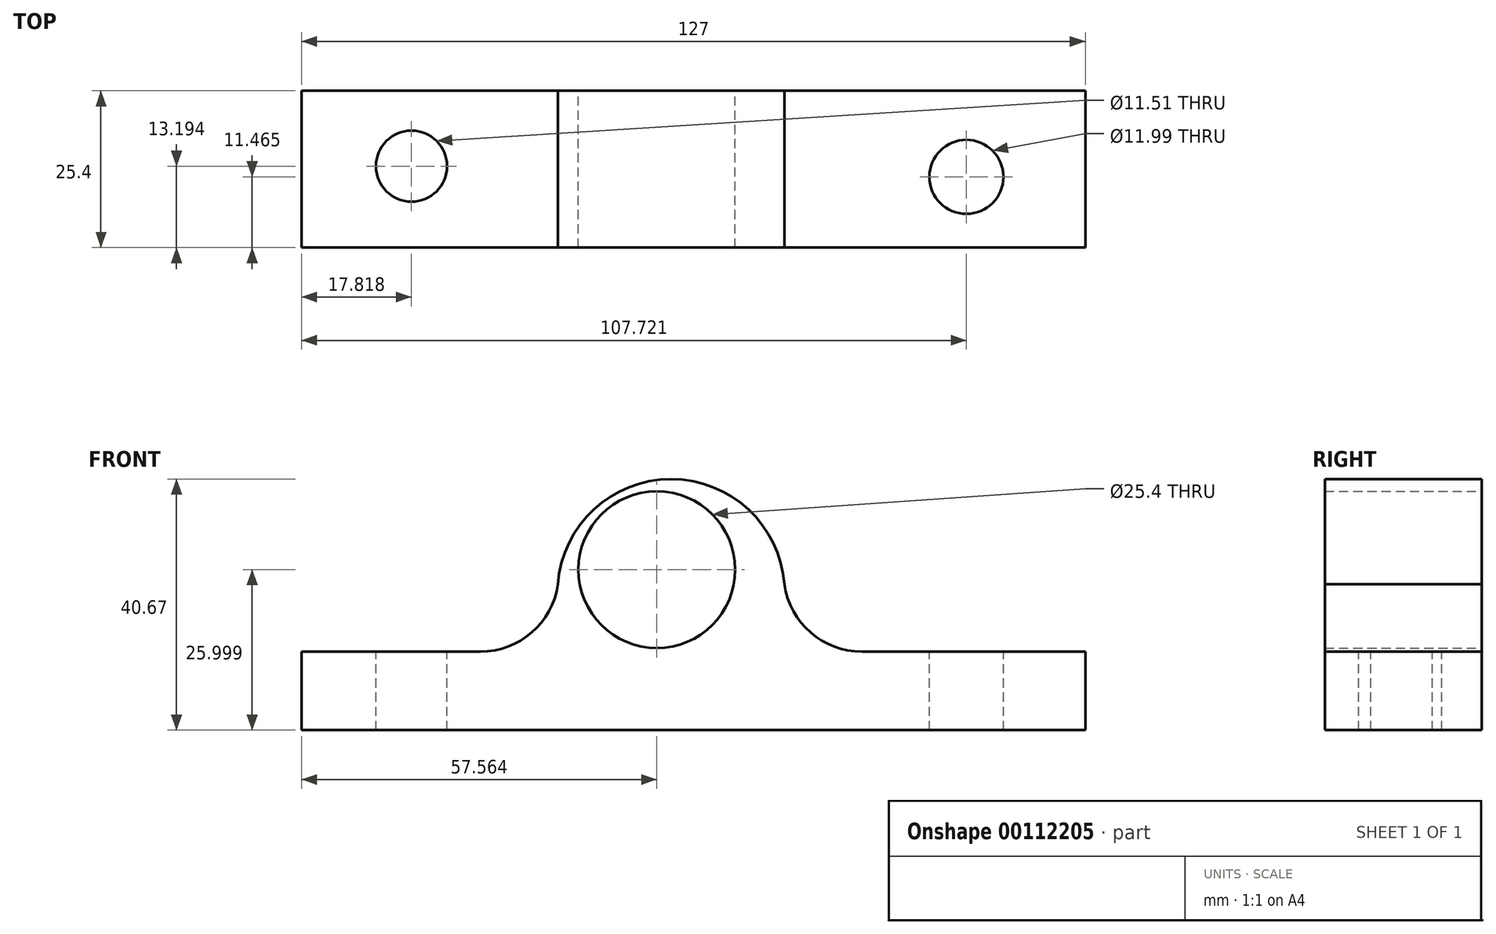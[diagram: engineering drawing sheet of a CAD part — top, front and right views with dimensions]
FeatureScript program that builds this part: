
annotation { "Feature Type Name" : "Feature", "Feature Type Description" : "" }
export const myFeature = defineFeature(function(context is Context, id is Id, definition is map)
    precondition{}
    {
        {
            var Q0;
            Q0=qCreatedBy(makeId("Front.planeOp"),FACE);
            var sketch = newSketch(context, id + "F0", { "sketchPlane" : qUnion([Q0])});
            skLineSegment(sketch, "E0", {"start": v(-62.5, -9.62) * mm, "end": v(-62.5, -22.32) * mm});
            skLineSegment(sketch, "E1", {"start": v(-62.5, -22.32) * mm, "end": v(64.5, -22.32) * mm});
            skLineSegment(sketch, "E2", {"start": v(64.5, -22.32) * mm, "end": v(64.5, -9.62) * mm});
            skLineSegment(sketch, "E3", {"start": v(64.5, -9.62) * mm, "end": v(28.3, -9.62) * mm});
            skLineSegment(sketch, "E4", {"start": v(-62.5, -9.62) * mm, "end": v(-33.54, -9.62) * mm});
            skArc(sketch, "E5.filletArc", {"start": v(-33.54, -9.62) * mm, "mid": v(-25.2, -6.5) * mm, "end": v(-20.96, 1.32) * mm});
            skArc(sketch, "E6.filletArc", {"start": v(15.73, 1.32) * mm, "mid": v(19.97, -6.5) * mm, "end": v(28.3, -9.62) * mm});
            skArc(sketch, "E7", {"start": v(15.73, 1.32) * mm, "mid": v(-2.62, 18.35) * mm, "end": v(-20.96, 1.32) * mm});
            skCircle(sketch, "E8", {"center": v(-4.94, 3.68) * mm, "radius": 12.7 * mm});
            skSolve(sketch);
        }
        {
            var Q0;
            Q0 = qSketchRegion(id + "F0", true);
            extrude(context, id + "F1", {"entities" : qUnion([Q0]), "depth" : 25.4 * mm});
        }
        {
            var Q0;
            Q0=makeQuery(id+"F1.opExtrude","SWEPT_FACE",FACE,{"disambiguationData":[OSD([sQuery(id+"F0.wireOp",EDGE,"E4")])]});
            var sketch = newSketch(context, id + "F2", { "sketchPlane" : qUnion([Q0])});
            skCircle(sketch, "E9", {"center": v(-44.68, -12.2) * mm, "radius": 5.75 * mm});
            skSolve(sketch);
        }
        {
            var Q0;
            Q0=makeQuery(id+"F1.opExtrude","SWEPT_FACE",FACE,{"disambiguationData":[OSD([sQuery(id+"F0.wireOp",EDGE,"E3")])]});
            var sketch = newSketch(context, id + "F3", { "sketchPlane" : qUnion([Q0])});
            skCircle(sketch, "E10", {"center": v(45.22, -13.94) * mm, "radius": 6 * mm});
            skSolve(sketch);
        }
        {
            var Q0;
            Q0 = qSketchRegion(id + "F2", true);
            extrude(context, id + "F4", {"entities" : qUnion([Q0]), "operationType" : NewBodyOperationType.REMOVE, "oppositeDirection" : true, "depth" : 25.4 * mm});
        }
        {
            var Q0;
            Q0=makeQuery(id+"F3.imprint","IMPRINT",FACE,{"disambiguationData":[TD([[makeQuery(id+"F3.imprint","IMPRINT",EDGE,{"derivedFrom":sQuery(id+"F3.wireOp",EDGE,"E10")}),1.0]])]});
            extrude(context, id + "F5", {"entities" : qUnion([Q0]), "operationType" : NewBodyOperationType.REMOVE, "oppositeDirection" : true, "depth" : 25.4 * mm});
        }
    });
